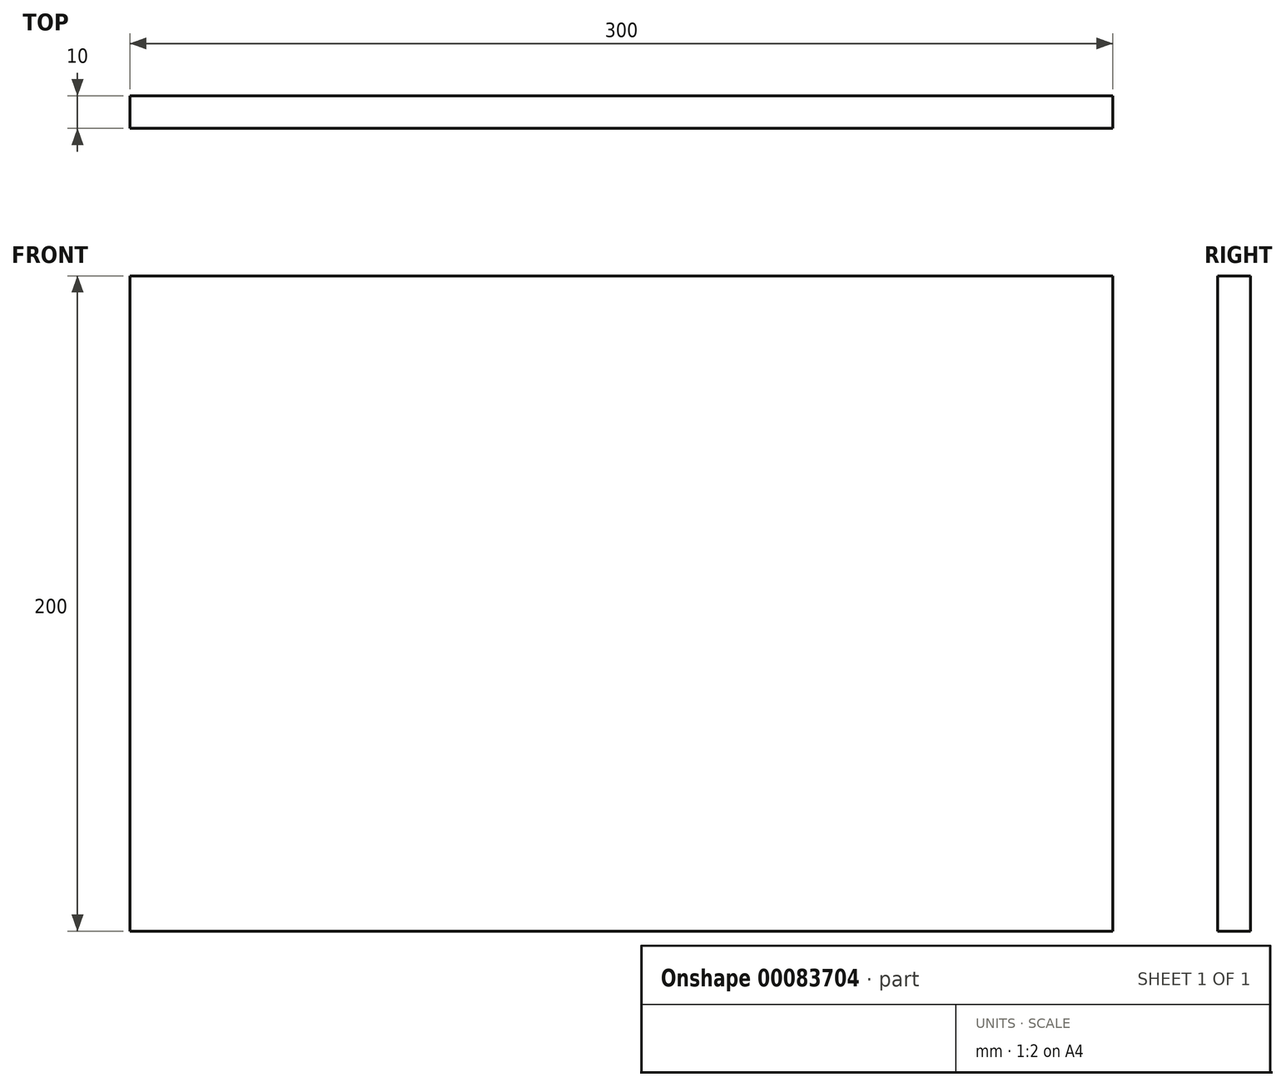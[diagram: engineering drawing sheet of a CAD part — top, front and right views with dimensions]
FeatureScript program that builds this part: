
annotation { "Feature Type Name" : "Feature", "Feature Type Description" : "" }
export const myFeature = defineFeature(function(context is Context, id is Id, definition is map)
    precondition{}
    {
        {
            var Q0;
            Q0=qCreatedBy(makeId("Front.planeOp"),FACE);
            var sketch = newSketch(context, id + "F0", { "sketchPlane" : qUnion([Q0])});
            skLineSegment(sketch, "E0.bottom", {"start": v(150, -100) * mm, "end": v(-150, -100) * mm});
            skLineSegment(sketch, "E0.top", {"start": v(150, 100) * mm, "end": v(-150, 100) * mm});
            skLineSegment(sketch, "E0.left", {"start": v(150, -100) * mm, "end": v(150, 100) * mm});
            skLineSegment(sketch, "E0.right", {"start": v(-150, -100) * mm, "end": v(-150, 100) * mm});
            skPoint(sketch, "E0.middle", {"position": v(0, 0) * mm});
            skSolve(sketch);
        }
        {
            var Q0;
            Q0=makeQuery(id+"F0.imprint","IMPRINT",FACE,{"disambiguationData":[TD([[makeQuery(id+"F0.imprint","IMPRINT",EDGE,{"derivedFrom":sQuery(id+"F0.wireOp",EDGE,"E0.bottom")}),-1.0]])]});
            extrude(context, id + "F1", {"entities" : qUnion([Q0]), "depth" : 10 * mm});
        }
    });
